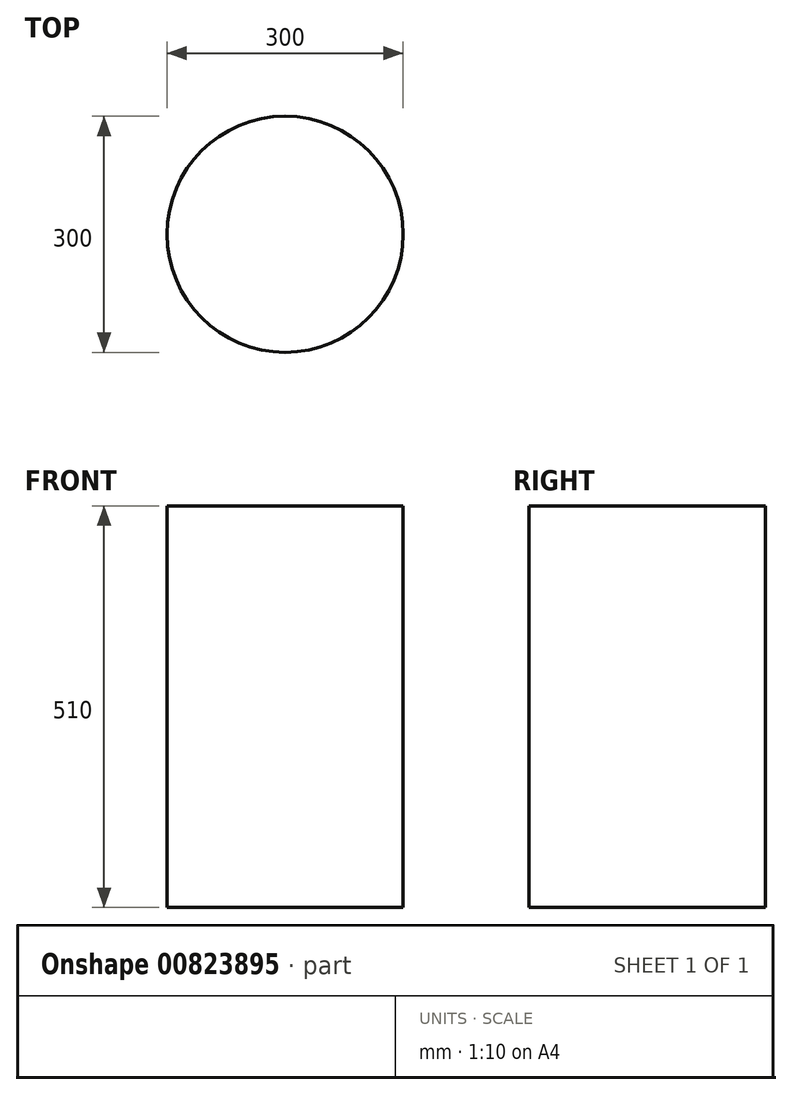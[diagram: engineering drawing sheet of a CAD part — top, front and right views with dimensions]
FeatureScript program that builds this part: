
annotation { "Feature Type Name" : "Feature", "Feature Type Description" : "" }
export const myFeature = defineFeature(function(context is Context, id is Id, definition is map)
    precondition{}
    {
        {
            var Q0;
            Q0=qCreatedBy(makeId("Front.planeOp"),FACE);
            var sketch = newSketch(context, id + "F0", { "sketchPlane" : qUnion([Q0])});
            skLineSegment(sketch, "E0.bottom", {"start": v(-150, 255) * mm, "end": v(150, 255) * mm});
            skLineSegment(sketch, "E0.top", {"start": v(-150, -255) * mm, "end": v(150, -255) * mm});
            skLineSegment(sketch, "E0.left", {"start": v(-150, 255) * mm, "end": v(-150, -255) * mm});
            skLineSegment(sketch, "E0.right", {"start": v(150, 255) * mm, "end": v(150, -255) * mm});
            skPoint(sketch, "E0.middle", {"position": v(0, 0) * mm});
            skLineSegment(sketch, "E1", {"start": v(0, 255) * mm, "end": v(0, -255) * mm});
            skSolve(sketch);
        }
        {
            var Q0;
            {var subQ0=sQuery(id+"F0.wireOp",EDGE,"E0.right");Q0=makeQuery(id+"F0.imprint","IMPRINT",FACE,{"disambiguationData":[TD([[makeQuery(id+"F0.imprint","IMPRINT",EDGE,{"derivedFrom":subQ0}),-1.0]])]});}
            var Q1;
            Q1=sQuery(id+"F0.wireOp",EDGE,"E1");
            revolve(context, id + "F1", {"surfaceOperationType" : NewSurfaceOperationType.NEW, "entities" : qUnion([Q0]), "axis" : qUnion([Q1]), "revolveType" : RevolveType.FULL});
        }
    });
